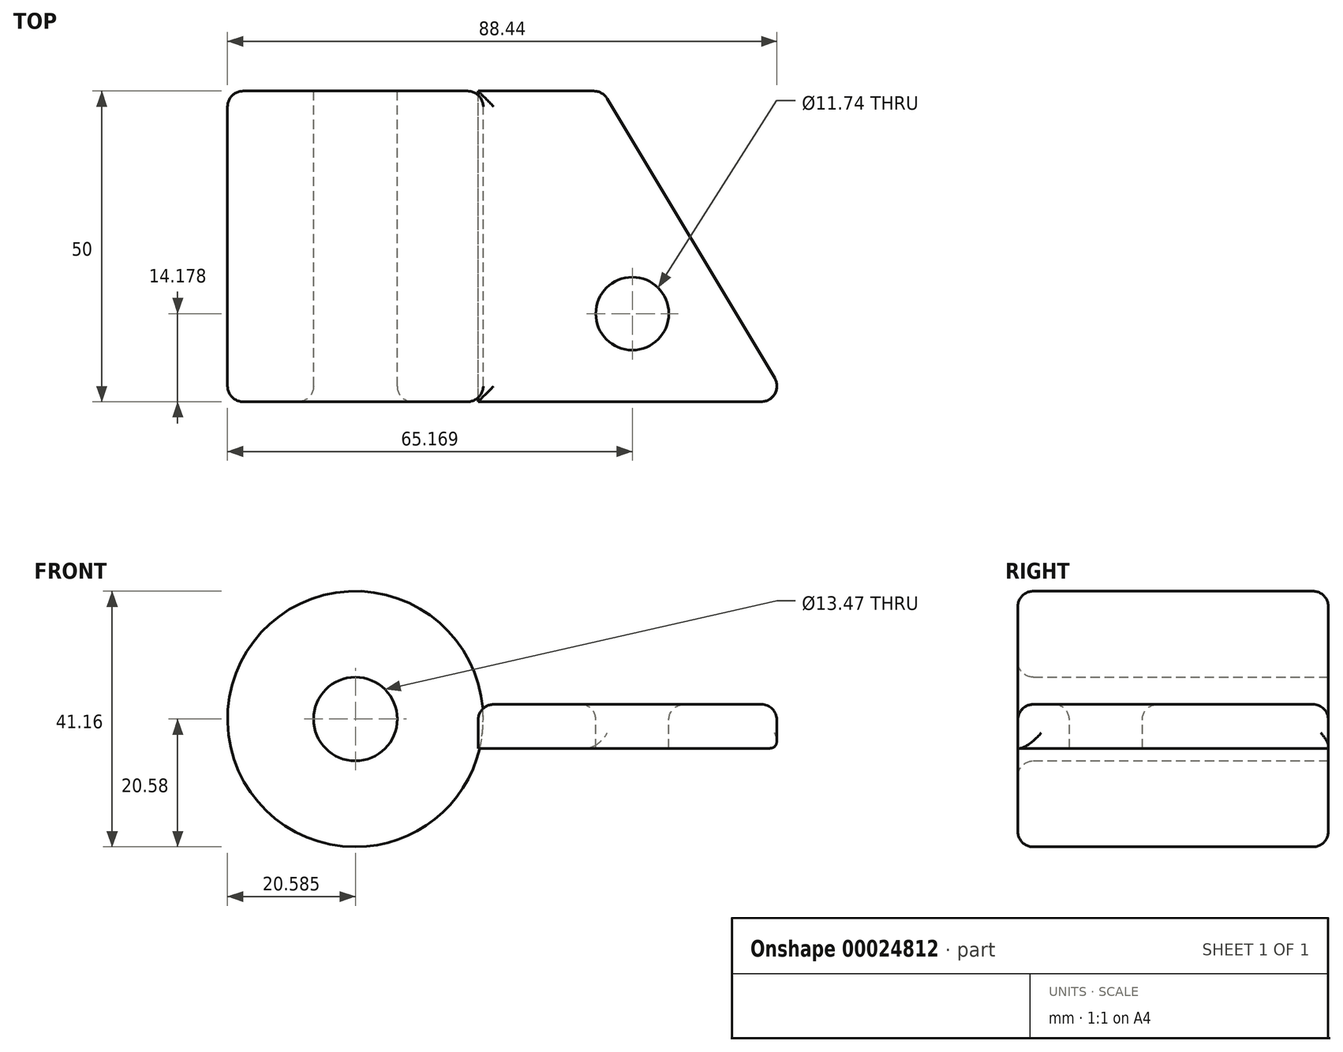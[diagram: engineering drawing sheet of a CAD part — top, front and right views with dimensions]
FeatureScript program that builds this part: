
annotation { "Feature Type Name" : "Feature", "Feature Type Description" : "" }
export const myFeature = defineFeature(function(context is Context, id is Id, definition is map)
    precondition{}
    {
        {
            var Q0;
            Q0=qCreatedBy(makeId("Front.planeOp"),FACE);
            var sketch = newSketch(context, id + "F0", { "sketchPlane" : qUnion([Q0])});
            skCircle(sketch, "E0", {"center": v(-44.76, 6.82) * mm, "radius": 20.58 * mm});
            skCircle(sketch, "E1", {"center": v(-44.76, 6.82) * mm, "radius": 6.74 * mm});
            skSolve(sketch);
        }
        {
            var Q0;
            Q0=makeQuery(id+"F0.imprint","IMPRINT",FACE,{"disambiguationData":[TD([[makeQuery(id+"F0.imprint","IMPRINT",EDGE,{"derivedFrom":sQuery(id+"F0.wireOp",EDGE,"E0")}),1.0]])]});
            extrude(context, id + "F1", {"entities" : qUnion([Q0]), "depth" : 50 * mm});
        }
        {
            var Q0;
            Q0=qCreatedBy(makeId("Right.planeOp"),FACE);
            var sketch = newSketch(context, id + "F2", { "sketchPlane" : qUnion([Q0])});
            skLineSegment(sketch, "E2.bottom", {"start": v(-50.14, 9.18) * mm, "end": v(0, 9.18) * mm});
            skLineSegment(sketch, "E2.top", {"start": v(-50.14, 2.1) * mm, "end": v(0, 2.1) * mm});
            skLineSegment(sketch, "E2.left", {"start": v(-50.14, 9.18) * mm, "end": v(-50.14, 2.1) * mm});
            skLineSegment(sketch, "E2.right", {"start": v(0, 9.18) * mm, "end": v(0, 2.1) * mm});
            skSolve(sketch);
        }
        {
            var Q0;
            Q0=makeQuery(id+"F2.imprint","IMPRINT",FACE,{"disambiguationData":[TD([[makeQuery(id+"F2.imprint","IMPRINT",EDGE,{"derivedFrom":sQuery(id+"F2.wireOp",EDGE,"E2.bottom")}),-1.0]])]});
            extrude(context, id + "F3", {"entities" : qUnion([Q0]), "oppositeDirection" : true, "depth" : 25 * mm});
        }
        {
            var Q0;
            Q0=makeQuery(id+"F3.opExtrude","CAP_FACE",FACE,{"disambiguationData":[OSD([sQuery(id+"F2.wireOp",EDGE,"E2.bottom"),sQuery(id+"F2.wireOp",EDGE,"E2.top"),sQuery(id+"F2.wireOp",EDGE,"E2.left"),sQuery(id+"F2.wireOp",EDGE,"E2.right")])],"isStart":true});
            extrude(context, id + "F4", {"entities" : qUnion([Q0]), "operationType" : NewBodyOperationType.ADD, "depth" : 25 * mm});
        }
        {
            var Q0;
            {var subQ0=sQuery(id+"F2.wireOp",EDGE,"E2.left");Q0=makeQuery(id+"F4.boolean.opBoolean","MERGE",FACE,{"derivedFrom":[makeQuery(id+"F3.opExtrude","SWEPT_FACE",FACE,{"disambiguationData":[OSD([subQ0])]}),makeQuery(id+"F4.opExtrude","SWEPT_FACE",FACE,{"disambiguationData":[OSD([subQ0])]})]});}
            var Q1;
            Q1=makeQuery(id+"F1.opExtrude","CAP_FACE",FACE,{"disambiguationData":[OSD([sQuery(id+"F0.wireOp",EDGE,"E0"),sQuery(id+"F0.wireOp",EDGE,"E1")])],"isStart":false});
            extrude(context, id + "F5", {"entities" : qUnion([Q0]), "operationType" : NewBodyOperationType.REMOVE, "endBound" : BoundingType.UP_TO_SURFACE, "oppositeDirection" : true, "endBoundEntityFace" : qUnion([Q1]), "depth" : 25 * mm});
        }
        {
            var Q0;
            {var subQ0=sQuery(id+"F2.wireOp",EDGE,"E2.bottom");Q0=makeQuery(id+"F4.boolean.opBoolean","MERGE",FACE,{"derivedFrom":[makeQuery(id+"F3.opExtrude","SWEPT_FACE",FACE,{"disambiguationData":[OSD([subQ0])]}),makeQuery(id+"F4.opExtrude","SWEPT_FACE",FACE,{"disambiguationData":[OSD([subQ0])]})]});}
            var sketch = newSketch(context, id + "F6", { "sketchPlane" : qUnion([Q0])});
            skLineSegment(sketch, "E3", {"start": v(25, -50) * mm, "end": v(-4.96, 0) * mm});
            skSolve(sketch);
        }
        {
            var Q0;
            {var subQ3=sQuery(id+"F6.wireOp",EDGE,"E3");Q0=makeQuery(id+"F6.imprint","IMPRINT",FACE,{"disambiguationData":[TD([[makeQuery(id+"F6.imprint","IMPRINT",EDGE,{"derivedFrom":subQ3}),-1.0]])]});}
            extrude(context, id + "F7", {"entities" : qUnion([Q0]), "operationType" : NewBodyOperationType.REMOVE, "endBound" : BoundingType.THROUGH_ALL, "oppositeDirection" : true, "depth" : 25 * mm});
        }
        {
            var Q0;
            {var subQ0=sQuery(id+"F2.wireOp",EDGE,"E2.bottom");Q0=makeQuery(id+"F4.boolean.opBoolean","MERGE",FACE,{"derivedFrom":[makeQuery(id+"F3.opExtrude","SWEPT_FACE",FACE,{"disambiguationData":[OSD([subQ0])]}),makeQuery(id+"F4.opExtrude","SWEPT_FACE",FACE,{"disambiguationData":[OSD([subQ0])]})]});}
            var sketch = newSketch(context, id + "F8", { "sketchPlane" : qUnion([Q0])});
            skCircle(sketch, "E4", {"center": v(-0.18, -35.82) * mm, "radius": 5.87 * mm});
            skSolve(sketch);
        }
        {
            var Q0;
            Q0=makeQuery(id+"F8.imprint","IMPRINT",FACE,{"disambiguationData":[TD([[makeQuery(id+"F8.imprint","IMPRINT",EDGE,{"derivedFrom":sQuery(id+"F8.wireOp",EDGE,"E4")}),1.0]])]});
            extrude(context, id + "F9", {"entities" : qUnion([Q0]), "operationType" : NewBodyOperationType.REMOVE, "endBound" : BoundingType.THROUGH_ALL, "oppositeDirection" : true, "depth" : 25 * mm});
        }
        {
            var Q0;
            Q0=makeQuery(id+"F5.boolean.opBoolean","MERGE",FACE,{"derivedFrom":[makeQuery(id+"F1.opExtrude","CAP_FACE",FACE,{"disambiguationData":[OSD([sQuery(id+"F0.wireOp",EDGE,"E0"),sQuery(id+"F0.wireOp",EDGE,"E1")])],"isStart":false}),makeQuery(id+"F5.opExtrude","CAP_FACE",FACE,{"disambiguationData":[OSD([sQuery(id+"F2.wireOp",EDGE,"E2.left")])],"isStart":false})]});
            var Q1;
            Q1=makeQuery(id+"F1.opExtrude","CAP_EDGE",EDGE,{"disambiguationData":[OSD([sQuery(id+"F0.wireOp",EDGE,"E1")])],"isStart":false});
            var Q2;
            Q2=makeQuery(id+"F9.boolean.opBoolean","COPY",EDGE,{"derivedFrom":makeQuery(id+"F9.opExtrude","CAP_EDGE",EDGE,{"disambiguationData":[OSD([sQuery(id+"F8.wireOp",EDGE,"E4")])],"isStart":true})});
            var Q3;
            {var subQ0=sQuery(id+"F2.wireOp",EDGE,"E2.bottom");Q3=makeQuery(id+"F4.boolean.opBoolean","MERGE",FACE,{"derivedFrom":[makeQuery(id+"F3.opExtrude","SWEPT_FACE",FACE,{"disambiguationData":[OSD([subQ0])]}),makeQuery(id+"F4.opExtrude","SWEPT_FACE",FACE,{"disambiguationData":[OSD([subQ0])]})]});}
            var Q4;
            Q4=makeQuery(id+"F1.opExtrude","SWEPT_FACE",FACE,{"disambiguationData":[OSD([sQuery(id+"F0.wireOp",EDGE,"E0")])]});
            var Q5;
            Q5=makeQuery(id+"F7.boolean.opBoolean","COPY",FACE,{"derivedFrom":makeQuery(id+"F7.opExtrude","SWEPT_FACE",FACE,{"disambiguationData":[OSD([sQuery(id+"F6.wireOp",EDGE,"E3")])]})});
            fillet(context, id + "F10", {"entities" : qUnion([Q0, Q1, Q2, Q3, Q4, Q5]), "radius" : 2.5 * mm, "tangentPropagation" : true, "allowEdgeOverflow" : false});
        }
    });
